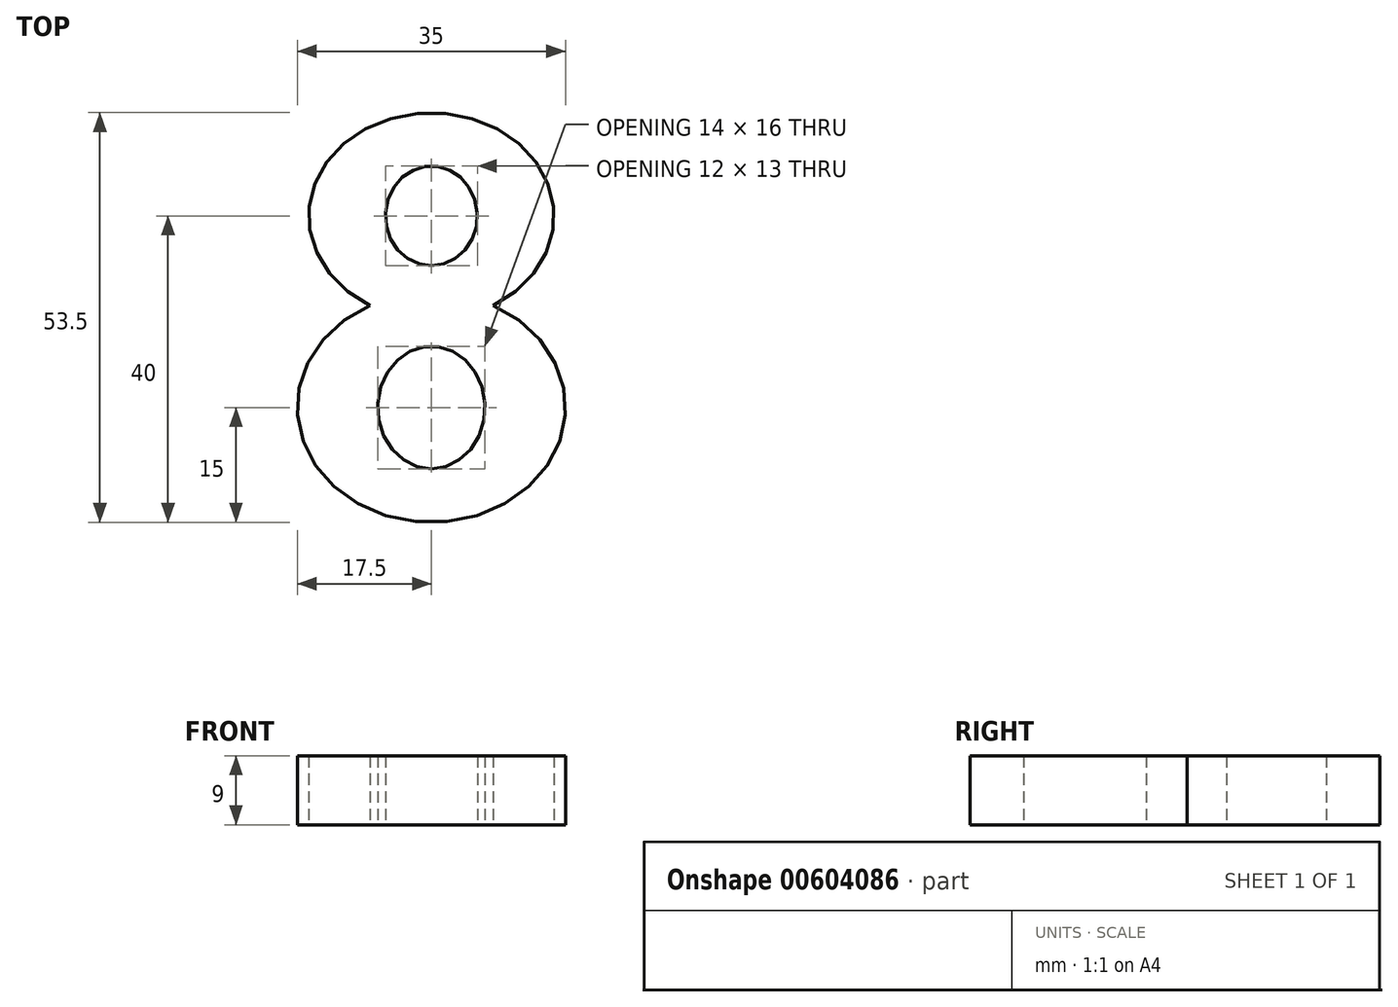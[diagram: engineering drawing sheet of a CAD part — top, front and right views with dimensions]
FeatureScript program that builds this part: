
annotation { "Feature Type Name" : "Feature", "Feature Type Description" : "" }
export const myFeature = defineFeature(function(context is Context, id is Id, definition is map)
    precondition{}
    {
        {
            var Q0;
            Q0=qCreatedBy(makeId("Top.planeOp"),FACE);
            var sketch = newSketch(context, id + "F0", { "sketchPlane" : qUnion([Q0])});
            skEllipticalArc(sketch, "E0", {});
            skEllipticalArc(sketch, "E1", {});
            skPoint(sketch, "E2", {"position": v(0, 11.5) * mm});
            skPoint(sketch, "E3", {"position": v(0, 15) * mm});
            skPoint(sketch, "E4", {"position": v(0, -15) * mm});
            skPoint(sketch, "E5", {"position": v(0, 38.5) * mm});
            skEllipse(sketch, "E6", {"center": v(0, 25) * mm, "majorRadius": 6.5 * mm, "minorRadius": 6 * mm, "majorAxis": v(0, -1)});
            skEllipse(sketch, "E7", {"center": v(0, 0) * mm, "majorRadius": 8 * mm, "minorRadius": 7 * mm, "majorAxis": v(0, -1)});
            const initialGuessF0  = {"E0": [0, 0, 1, 0, 0.0175, 0.015, 2.0478043632290612, 1.0937882903607319], "E1": [0, 0.025, -1, 0, 0.016, 0.0135, 2.0968980657512333, 1.0446945878385607]};
            skSetInitialGuess(sketch, initialGuessF0);
            skSolve(sketch);
        }
        {
            var Q0;
            Q0=makeQuery(id+"F0.imprint","IMPRINT",FACE,{"disambiguationData":[TD([[makeQuery(id+"F0.imprint","IMPRINT",EDGE,{"derivedFrom":sQuery(id+"F0.wireOp",EDGE,"E0")}),1.0]])]});
            extrude(context, id + "F1", {"entities" : qUnion([Q0]), "depth" : 9 * mm, "offsetDistance" : 25 * mm});
        }
    });
